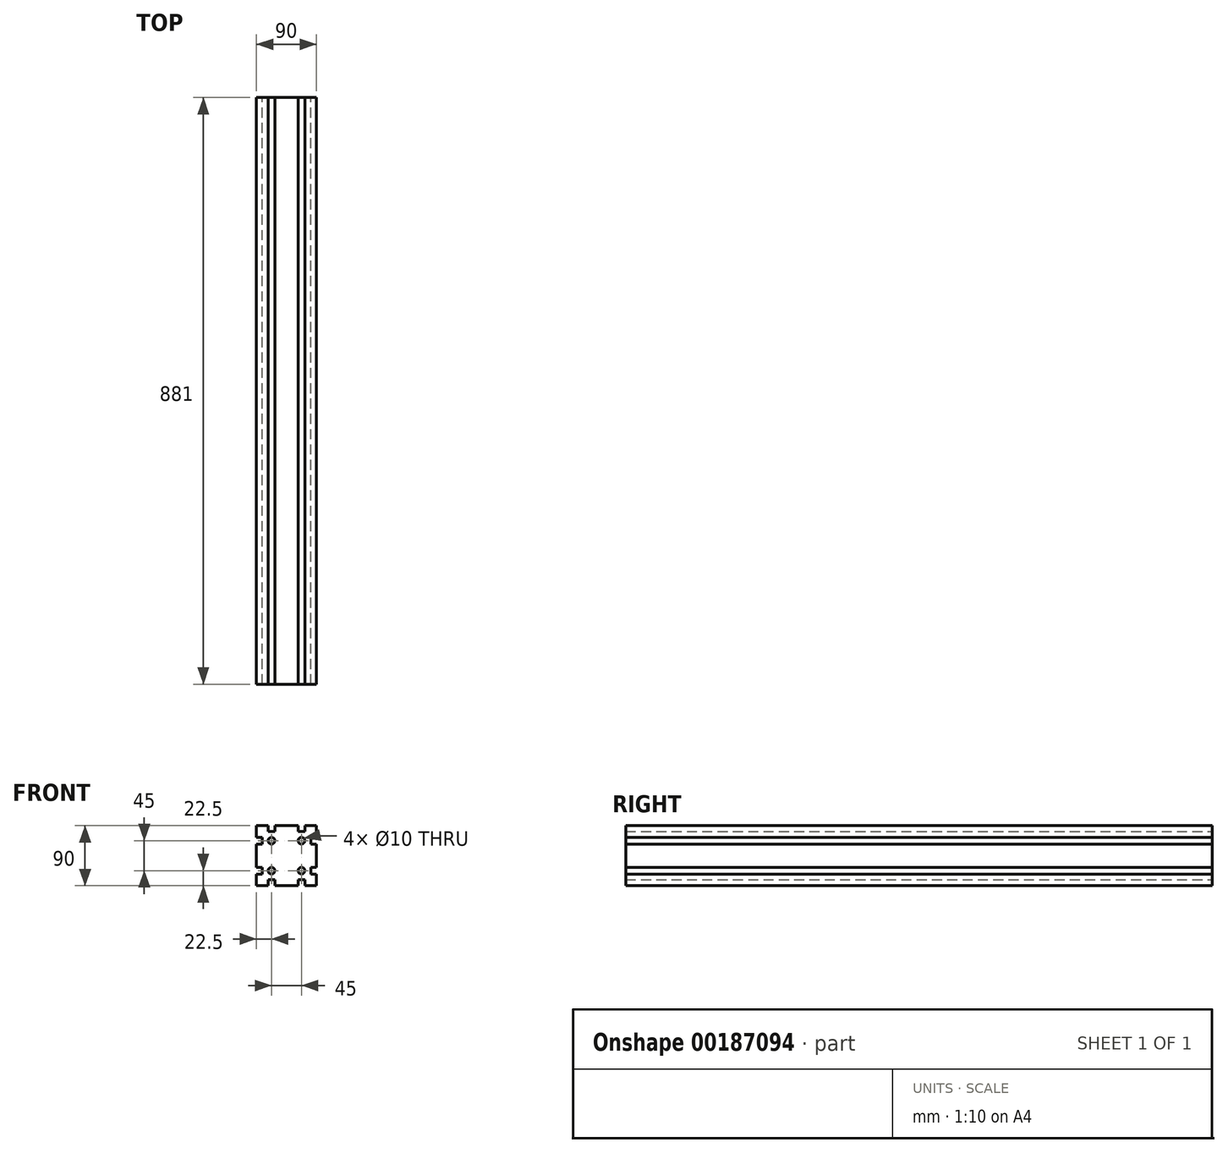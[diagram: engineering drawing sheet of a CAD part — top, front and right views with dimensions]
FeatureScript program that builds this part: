
annotation { "Feature Type Name" : "Feature", "Feature Type Description" : "" }
export const myFeature = defineFeature(function(context is Context, id is Id, definition is map)
    precondition{}
    {
        {
            var Q0;
            Q0=qCreatedBy(makeId("Front.planeOp"),FACE);
            var sketch = newSketch(context, id + "F0", { "sketchPlane" : qUnion([Q0])});
            skLineSegment(sketch, "E0.bottom", {"start": v(45, -45) * mm, "end": v(36.25, -45) * mm});
            skLineSegment(sketch, "E0.top", {"start": v(45, 45) * mm, "end": v(27.5, 45) * mm});
            skLineSegment(sketch, "E0.left", {"start": v(45, -45) * mm, "end": v(45, -27.5) * mm});
            skLineSegment(sketch, "E0.right", {"start": v(-45, -45) * mm, "end": v(-45, -27.5) * mm});
            skPoint(sketch, "E0.middle", {"position": v(0, 0) * mm});
            skCircle(sketch, "E1", {"center": v(-22.5, 22.5) * mm, "radius": 5 * mm});
            skCircle(sketch, "E2", {"center": v(22.5, 22.5) * mm, "radius": 5 * mm});
            skCircle(sketch, "E3", {"center": v(22.5, -22.5) * mm, "radius": 5 * mm});
            skCircle(sketch, "E4", {"center": v(-22.5, -22.5) * mm, "radius": 5 * mm});
            skLineSegment(sketch, "E5", {"start": v(-27.5, 45) * mm, "end": v(-27.5, 36.25) * mm});
            skLineSegment(sketch, "E6", {"start": v(-17.5, 45) * mm, "end": v(-17.5, 36.25) * mm});
            skLineSegment(sketch, "E7", {"start": v(17.5, 45) * mm, "end": v(17.5, 36.25) * mm});
            skLineSegment(sketch, "E8", {"start": v(27.5, 45) * mm, "end": v(27.5, 36.25) * mm});
            skLineSegment(sketch, "E9", {"start": v(-45, 27.5) * mm, "end": v(-36.25, 27.5) * mm});
            skLineSegment(sketch, "E10", {"start": v(-45, 17.5) * mm, "end": v(-36.25, 17.5) * mm});
            skLineSegment(sketch, "E11", {"start": v(-45, -17.5) * mm, "end": v(-36.25, -17.5) * mm});
            skLineSegment(sketch, "E12", {"start": v(-45, -27.5) * mm, "end": v(-36.25, -27.5) * mm});
            skLineSegment(sketch, "E13", {"start": v(-36.25, 27.5) * mm, "end": v(-36.25, 17.5) * mm});
            skLineSegment(sketch, "E14", {"start": v(36.25, 27.5) * mm, "end": v(36.25, 17.5) * mm});
            skLineSegment(sketch, "E15.trimOffspring", {"start": v(-45, 27.5) * mm, "end": v(-45, 45) * mm});
            skLineSegment(sketch, "E16.trimOffspring", {"start": v(45, 27.5) * mm, "end": v(45, 45) * mm});
            skLineSegment(sketch, "E17.trimOffspring", {"start": v(-27.5, 45) * mm, "end": v(-45, 45) * mm});
            skLineSegment(sketch, "E18.trimOffspring", {"start": v(17.5, 45) * mm, "end": v(-17.5, 45) * mm});
            skLineSegment(sketch, "E19.trimOffspring", {"start": v(-27.5, -45) * mm, "end": v(-45, -45) * mm});
            skLineSegment(sketch, "E20.trimOffspring", {"start": v(17.5, -45) * mm, "end": v(-17.5, -45) * mm});
            skLineSegment(sketch, "E21.trimOffspring", {"start": v(-45, -17.5) * mm, "end": v(-45, 17.5) * mm});
            skLineSegment(sketch, "E22.trimOffspring", {"start": v(45, -17.5) * mm, "end": v(45, 17.5) * mm});
            skLineSegment(sketch, "E23.trimOffspring", {"start": v(-36.25, -17.5) * mm, "end": v(-36.25, -27.5) * mm});
            skLineSegment(sketch, "E24.trimOffspring", {"start": v(36.25, -17.5) * mm, "end": v(36.25, -27.5) * mm});
            skLineSegment(sketch, "E25.trimOffspring", {"start": v(36.25, 17.5) * mm, "end": v(45, 17.5) * mm});
            skLineSegment(sketch, "E26.trimOffspring", {"start": v(36.25, 27.5) * mm, "end": v(45, 27.5) * mm});
            skPoint(sketch, "E27.orphan", {"position": v(36.25, 45) * mm});
            skPoint(sketch, "E28.trimOffspring.end.orphan", {"position": v(45, 36.25) * mm});
            skLineSegment(sketch, "E29.trimOffspring", {"start": v(17.5, 36.25) * mm, "end": v(27.5, 36.25) * mm});
            skLineSegment(sketch, "E30", {"start": v(27.5, -45) * mm, "end": v(36.25, -45) * mm});
            skPoint(sketch, "E31.orphan", {"position": v(45, -36.25) * mm});
            skLineSegment(sketch, "E32.trimOffspring", {"start": v(36.25, -27.5) * mm, "end": v(45, -27.5) * mm});
            skLineSegment(sketch, "E33.trimOffspring", {"start": v(27.5, -36.25) * mm, "end": v(27.5, -45) * mm});
            skLineSegment(sketch, "E34.trimOffspring", {"start": v(17.5, -36.25) * mm, "end": v(17.5, -45) * mm});
            skLineSegment(sketch, "E35.trimOffspring", {"start": v(36.25, -17.5) * mm, "end": v(45, -17.5) * mm});
            skLineSegment(sketch, "E36.trimOffspring", {"start": v(17.5, -36.25) * mm, "end": v(27.5, -36.25) * mm});
            skLineSegment(sketch, "E37.trimOffspring", {"start": v(-27.5, -36.25) * mm, "end": v(-27.5, -45) * mm});
            skLineSegment(sketch, "E38.trimOffspring", {"start": v(-17.5, -36.25) * mm, "end": v(-17.5, -45) * mm});
            skLineSegment(sketch, "E39.trimOffspring", {"start": v(-27.5, -36.25) * mm, "end": v(-17.5, -36.25) * mm});
            skLineSegment(sketch, "E40.trimOffspring", {"start": v(-27.5, 36.25) * mm, "end": v(-17.5, 36.25) * mm});
            skPoint(sketch, "E41.orphan", {"position": v(-36.25, 45) * mm});
            skSolve(sketch);
        }
        {
            var Q0;
            Q0=makeQuery(id+"F0.imprint","IMPRINT",FACE,{"disambiguationData":[TD([[makeQuery(id+"F0.imprint","IMPRINT",EDGE,{"derivedFrom":sQuery(id+"F0.wireOp",EDGE,"E0.bottom")}),-1.0]])]});
            extrude(context, id + "F1", {"entities" : qUnion([Q0]), "depth" : 881 * mm});
        }
    });
